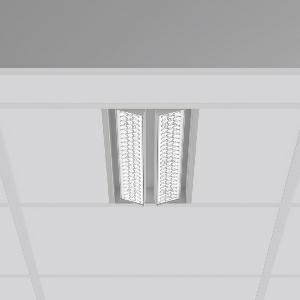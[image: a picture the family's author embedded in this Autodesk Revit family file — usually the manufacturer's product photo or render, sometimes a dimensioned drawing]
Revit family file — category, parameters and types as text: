
# Revit family: tx-move_901736_004_76_1ead
name_source: partatom
category: Lighting Fixtures
units: mm (PartAtom-declared; Revit-internal decimal feet)

## family parameters
Cut with Voids When Loaded = No
Host = Face
Light Source = No
Part Type = Normal
Room Calculation Point = No
Round Connector Dimension = Use Diameter
Shared = No

## types (1)
- MultiLumen 1 (1 x LED Modul 830, 2750 lm, 3000)
    Apparent Load = 35 VA
    Approval mark = CE
    CIE Flux Codes = 90 97 99 100 100
    Color Rendering = 80
    Color Temperature = 3000
    Default Elevation = 1800 mm
    Description = Series: TX-MOVE
Einlege/Einbau-Flächenstrahler. Housing: sheet steel, powder-coated. 2xSwivel range: 90°. High-efficiency LED units with optimum light control thanks to clear plastic (PC) lens optics. Spezielle Mikrostrukturen reduzieren Gelbsaum. Symmetrical light distribution. Suitable for laying in grid ceiling module 625. Connected converter included in separate gearbox.Suitable for through-wiring.MultiLumen: Luminous flux adjustable in 3 steps. Accessories: Mounting frame for installation in suspended ceilings. Environmentally friendly and resource-saving due to replaceable and recyclable components. 
Colour: silver, matt (approx. RAL 9006)
Length: 622 mm
Width: 190 mm
Height: 39 mm
Cut-out length: 602 mm
Cut-out width: 174 mm
Recess height: 100 mm
Lamp: LED
Socket: without socket
Colour temperature: 3000K
Colour rendering index (CRI): 80
System power: 35 W
Rated luminous flux: 5500 lm
Luminous efficiency: 157 lm/W
System power 2: 47 W
Rated luminous flux 2: 7100 lm
Luminous efficiency 2: 151 lm/W
System power 3: 68 W
Rated luminous flux 3: 9700 lm
Luminous efficiency 3: 143 lm/W
Control gear: Dimmable EVG, DALI
Protection class: I
Type of protection: IP 20
    Height = 0 mm  [stored 0 ft]
    Lamp = 1 x LED Modul 830
    Lamp Light Flux = 2750 lm
    Lamp count = 1
    Length = 622 mm
    Lifetime = 50000 h
    Luminous efficacy = 157 lm/W
    Manufacturer = RZB
    ModVariant = No
    Model = 901736.004.76
    Mounting Place = Ceiling, Wall
    Mounting Type = Recessed
    Number of Poles = 1
    OnlyDefault = Yes
    Power Factor = 1
    Product Name = TX-MOVE
    Product group = Recessed projectors
    ProductGroupID = 401
    Protection Class = Protection class I
    Protection Degree = IP 20
    RLX_Detail_Level = 1
    RLX_Emergency_Light_Flux = 0 lm
    RLX_Emergency_Type = 0
    RLX_Emergency_Type_DB = No
    RlxData = <blob elided: 34425 chars, md5=bbcc4808>
    Socket = socket
    Standby Power = 0 W
    System Light Flux = 5500 lm
    System Power = 35 W
    Type Comments = MultiLumen 1
    Type Image = 901737.004.jpg
    URL = http://relux.com
    VarID = multilumen_1
    Voltage = 230 V
    Voltage Range = 220-240 V
    Weight = 0.00 kg
    Width = 190 mm

note: [stored X ft] marks values corroborated as IEEE doubles in the binary element streams (Revit-internal decimal feet)

## geometry (parser evidence)
native form markers: Blend x4, Sweep x14
no freeform markers — native parametric forms only
